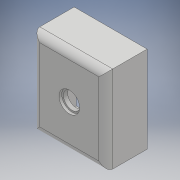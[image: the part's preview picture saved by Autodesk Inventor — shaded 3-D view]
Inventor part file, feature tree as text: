
AUTODESK INVENTOR PART (.ipt)
format: ipt  version: 2018 (Build 220112000, 112)  size: 122,368 bytes
history: native  units: mm
features: extrude x4, sketch x4, fillet x1
ambient origin geometry x8: Origin, YZ Plane, XZ Plane, XY Plane, X Axis, Y Axis, Z Axis, Center Point
bodies: Solid1 (feature_tree)
feature tree (9):
  extrude  "Extrusion1"  Depth=63.0mm
  extrude  "Extrusion2"  Depth=50.0mm
  extrude  "Extrusion3"  Depth=25.0mm TaperAngle=0.0deg
  extrude  "Extrusion4"  Depth=2.0mm TaperAngle=0.0deg
  fillet  "Fillet1"  Radius=12.5mm
  sketch  "Sketch1"  dims[d0=53.0mm d1=63.0mm]
  sketch  "Sketch2"  dims[d2=30.0mm d3=0.0mm d4=50.0mm]
  sketch  "Sketch3"  dims[d5=60.0mm d6=25.0mm d7=0.0mm]
  sketch  "Sketch4"  dims[d10=15.0mm d11=2.0mm d12=0.0mm d13=12.5mm d14=2.0mm d15=0.0mm d16=5.0mm]
